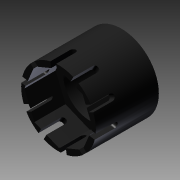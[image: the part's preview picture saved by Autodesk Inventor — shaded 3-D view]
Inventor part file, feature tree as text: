
AUTODESK INVENTOR PART (.ipt)
format: ipt  version: 2011 (Build 150239000, 239)  size: 166,912 bytes
history: native  units: mm (DEFAULTED — no unit token found)
features: extrude x4, sketch x4, fillet x1, pattern_circular x1
ambient origin geometry x8: Origin, YZ Plane, XZ Plane, XY Plane, X Axis, Y Axis, Z Axis, Center Point
bodies: Solid1 (feature_tree)
feature tree (10):
  extrude  "Extrusion1"  Depth=38.1mm TaperAngle=0.0deg
  extrude  "Extrusion2"  Depth=38.1mm TaperAngle=0.0deg
  extrude  "Extrusion3"  Depth=18.796mm TaperAngle=0.0deg
  extrude  "Extrusion4"  Depth=13.462mm TaperAngle=0.0deg
  fillet  "Fillet1"  Radius=1.651mm
  pattern_circular  "Circular Pattern1"  Count=10 Angle=360.0deg
  sketch  "Sketch1"  dims[d0=45.212mm d1=38.1mm d2=0.0mm]
  sketch  "Sketch2"  dims[d3=31.75mm d4=38.1mm d5=0.0mm]
  sketch  "Sketch3"  dims[d6=38.1mm d7=18.796mm d8=0.0mm]
  sketch  "Sketch4"  dims[d9=3.556mm d10=13.462mm d11=0.0mm d12=1.651mm d13=100.0mm d15=360.0deg]
